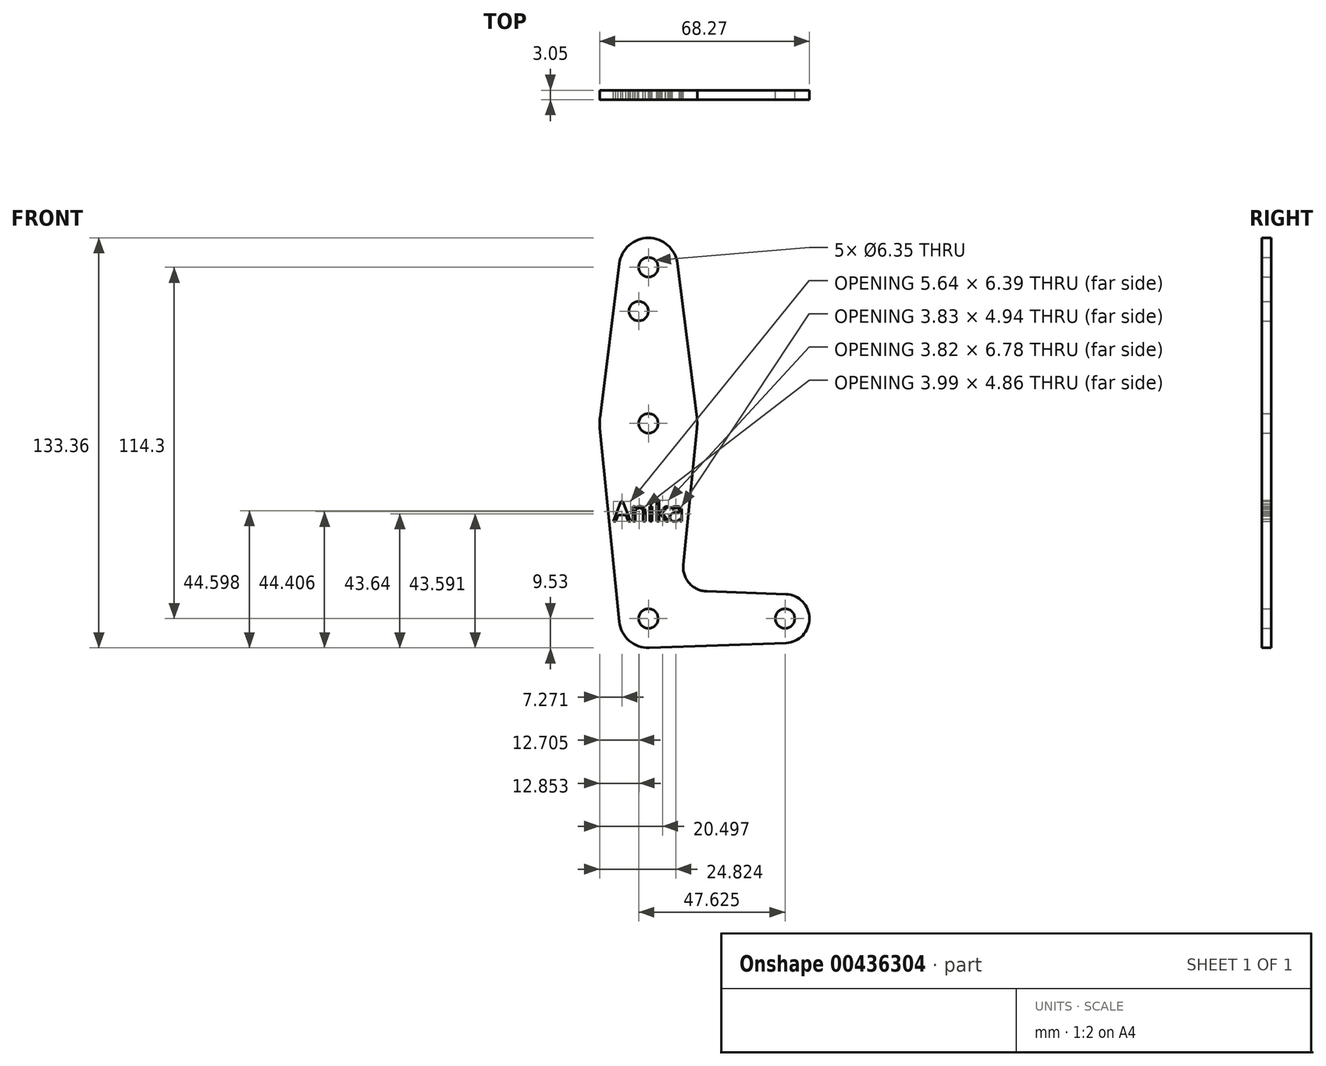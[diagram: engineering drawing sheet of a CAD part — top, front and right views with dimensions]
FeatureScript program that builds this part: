
annotation { "Feature Type Name" : "Feature", "Feature Type Description" : "" }
export const myFeature = defineFeature(function(context is Context, id is Id, definition is map)
    precondition{}
    {
        {
            var Q0;
            Q0=qCreatedBy(makeId("Front.planeOp"),FACE);
            var sketch = newSketch(context, id + "F0", { "sketchPlane" : qUnion([Q0])});
            skLineSegment(sketch, "E0", {"start": v(0, 0) * mm, "end": v(0, 114.3) * mm, "construction": true});
            skLineSegment(sketch, "E1", {"start": v(0, 0) * mm, "end": v(44.45, 0) * mm, "construction": true});
            skCircle(sketch, "E2", {"center": v(0, 114.3) * mm, "radius": 9.53 * mm});
            skCircle(sketch, "E3", {"center": v(0, 63.5) * mm, "radius": 15.88 * mm});
            skCircle(sketch, "E4", {"center": v(0, 0) * mm, "radius": 9.53 * mm});
            skCircle(sketch, "E5", {"center": v(44.45, 0) * mm, "radius": 7.94 * mm});
            skLineSegment(sketch, "E6", {"start": v(-9.45, 115.5) * mm, "end": v(-15.75, 65.48) * mm});
            skLineSegment(sketch, "E7", {"start": v(9.45, 115.5) * mm, "end": v(15.75, 65.48) * mm});
            skLineSegment(sketch, "E8", {"start": v(-15.8, 61.91) * mm, "end": v(-9.48, -0.95) * mm});
            skLineSegment(sketch, "E9", {"start": v(15.8, 61.91) * mm, "end": v(11.34, 17.6) * mm});
            skLineSegment(sketch, "E10", {"start": v(0.34, -9.52) * mm, "end": v(44.73, -7.93) * mm});
            skLineSegment(sketch, "E11", {"start": v(18.97, 8.85) * mm, "end": v(44.73, 7.93) * mm});
            skCircle(sketch, "E12", {"center": v(0, 114.3) * mm, "radius": 3.18 * mm});
            skCircle(sketch, "E13", {"center": v(-3.18, 100.03) * mm, "radius": 3.18 * mm});
            skCircle(sketch, "E14", {"center": v(0, 63.5) * mm, "radius": 3.18 * mm});
            skCircle(sketch, "E15", {"center": v(0, 0) * mm, "radius": 3.18 * mm});
            skCircle(sketch, "E16", {"center": v(44.45, 0) * mm, "radius": 3.18 * mm});
            skArc(sketch, "E17.filletArc", {"start": v(11.34, 17.6) * mm, "mid": v(13.26, 11.57) * mm, "end": v(18.97, 8.85) * mm});
            skText(sketch, "E18", { "text": "Anika", "fontName": "OpenSans-Regular.ttf"});
            const initialGuessF0  = {"E18": [-0.01143, 0.03168, 1, 0, 0.00642]};
            skSetInitialGuess(sketch, initialGuessF0);
            skSolve(sketch);
        }
        {
            var Q0;
            Q0 = qSketchRegion(id + "F0", true);
            extrude(context, id + "F1", {"entities" : qUnion([Q0]), "depth" : 3.05 * mm});
        }
    });
